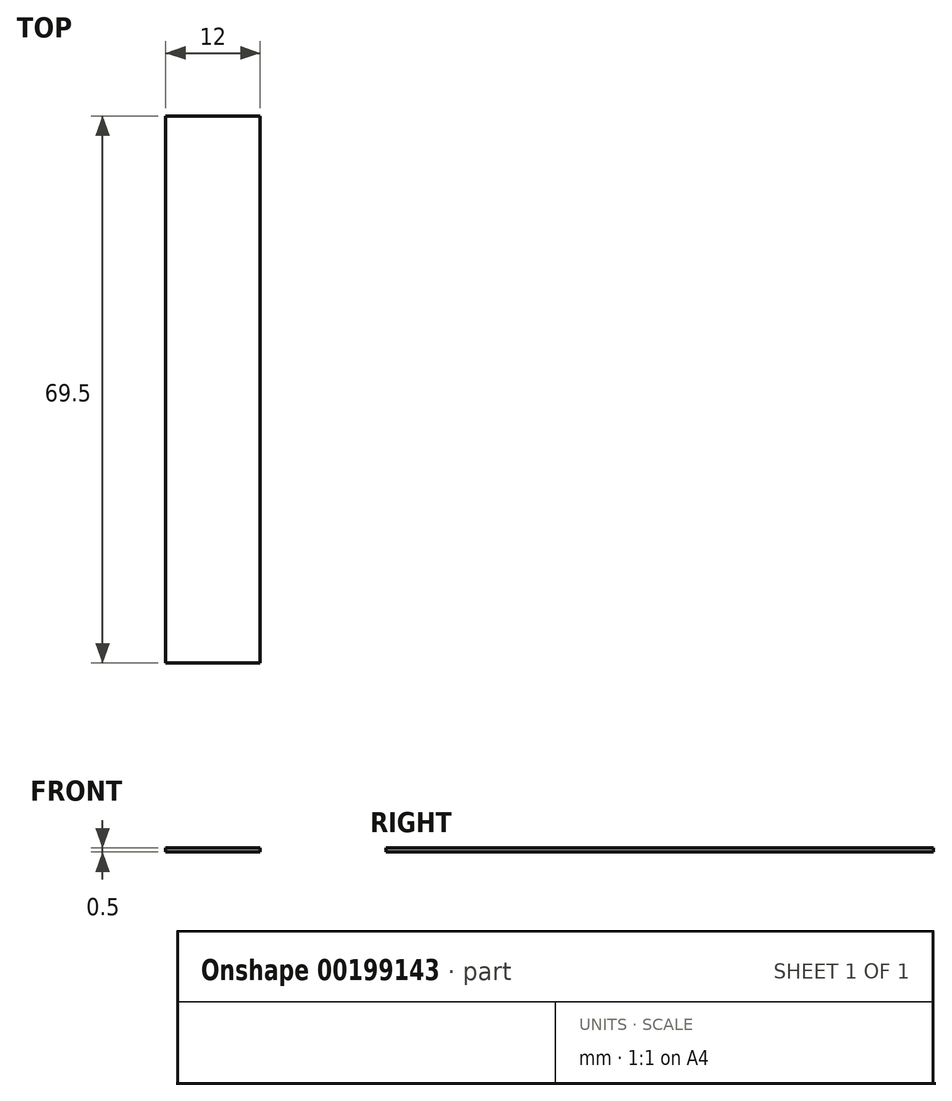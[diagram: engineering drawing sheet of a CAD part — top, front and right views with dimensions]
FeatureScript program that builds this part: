
annotation { "Feature Type Name" : "Feature", "Feature Type Description" : "" }
export const myFeature = defineFeature(function(context is Context, id is Id, definition is map)
    precondition{}
    {
        {
            var Q0;
            Q0=qCreatedBy(makeId("Top.planeOp"),FACE);
            var sketch = newSketch(context, id + "F0", { "sketchPlane" : qUnion([Q0])});
            skLineSegment(sketch, "E0.bottom", {"start": v(6, -34.75) * mm, "end": v(-6, -34.75) * mm});
            skLineSegment(sketch, "E0.top", {"start": v(6, 34.75) * mm, "end": v(-6, 34.75) * mm});
            skLineSegment(sketch, "E0.left", {"start": v(6, -34.75) * mm, "end": v(6, 34.75) * mm});
            skLineSegment(sketch, "E0.right", {"start": v(-6, -34.75) * mm, "end": v(-6, 34.75) * mm});
            skPoint(sketch, "E0.middle", {"position": v(0, 0) * mm});
            skSolve(sketch);
        }
        {
            var Q0;
            Q0 = qSketchRegion(id + "F0", true);
            extrude(context, id + "F1", {"entities" : qUnion([Q0]), "depth" : 0.5 * mm});
        }
    });
